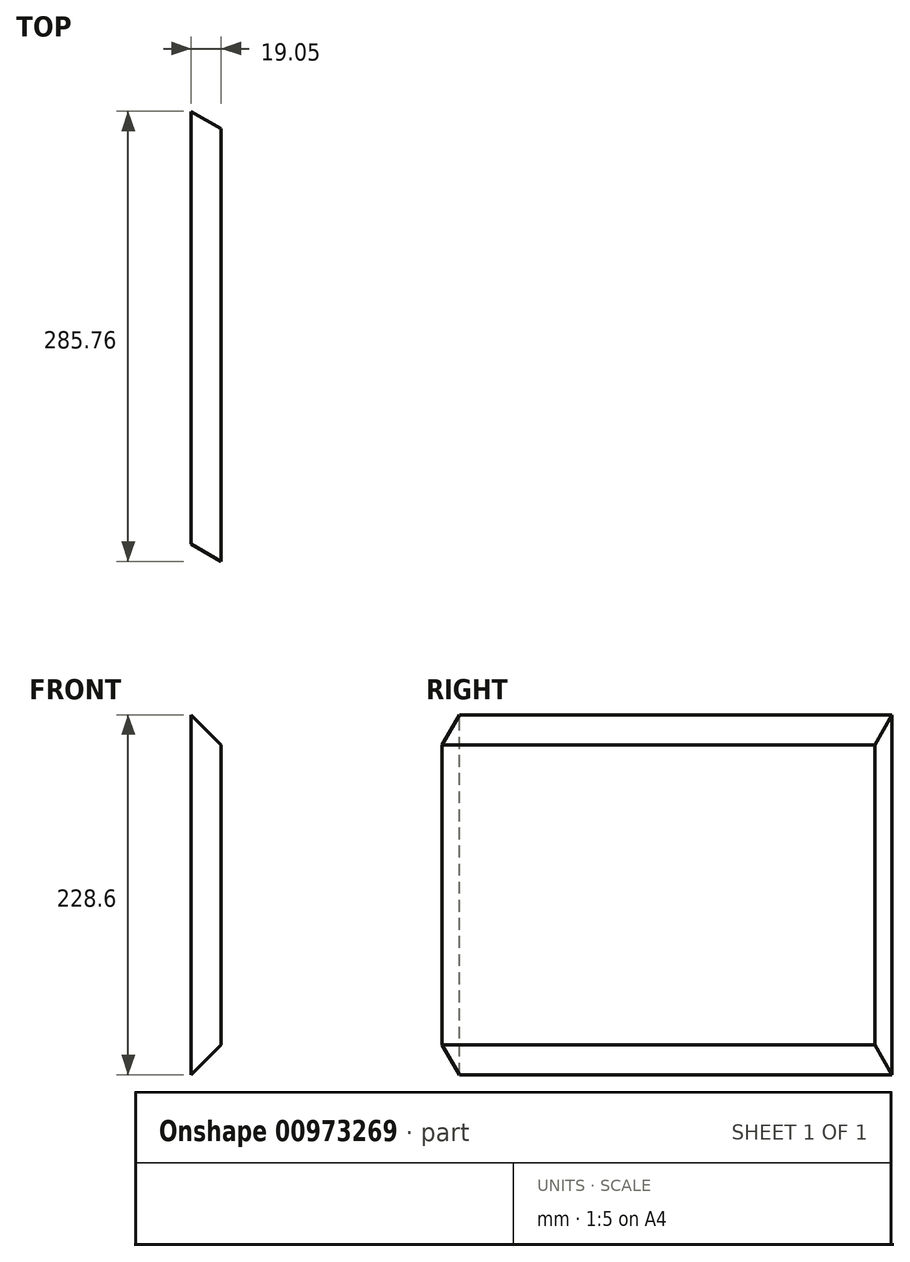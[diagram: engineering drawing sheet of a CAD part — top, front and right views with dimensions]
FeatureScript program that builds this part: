
annotation { "Feature Type Name" : "Feature", "Feature Type Description" : "" }
export const myFeature = defineFeature(function(context is Context, id is Id, definition is map)
    precondition{}
    {
        {
            var Q0;
            Q0=qCreatedBy(makeId("Right.planeOp"),FACE);
            var sketch = newSketch(context, id + "F0", { "sketchPlane" : qUnion([Q0])});
            skLineSegment(sketch, "E0.bottom", {"start": v(142.88, -114.3) * mm, "end": v(-142.88, -114.3) * mm});
            skLineSegment(sketch, "E0.top", {"start": v(142.88, 114.3) * mm, "end": v(-142.88, 114.3) * mm});
            skLineSegment(sketch, "E0.left", {"start": v(142.88, -114.3) * mm, "end": v(142.88, 114.3) * mm});
            skLineSegment(sketch, "E0.right", {"start": v(-142.88, -114.3) * mm, "end": v(-142.88, 114.3) * mm});
            skPoint(sketch, "E0.middle", {"position": v(0, 0) * mm});
            skSolve(sketch);
        }
        {
            var Q0;
            Q0=makeQuery(id+"F0.imprint","IMPRINT",FACE,{"disambiguationData":[TD([[makeQuery(id+"F0.imprint","IMPRINT",EDGE,{"derivedFrom":sQuery(id+"F0.wireOp",EDGE,"E0.bottom")}),-1.0]])]});
            extrude(context, id + "F1", {"entities" : qUnion([Q0]), "depth" : 19.05 * mm, "offsetDistance" : 25.4 * mm});
        }
        {
            var Q0;
            Q0=makeQuery(id+"F1.opExtrude","SWEPT_FACE",FACE,{"disambiguationData":[OSD([sQuery(id+"F0.wireOp",EDGE,"E0.top")])]});
            var sketch = newSketch(context, id + "F2", { "sketchPlane" : qUnion([Q0])});
            skLineSegment(sketch, "E1", {"start": v(19.05, -142.88) * mm, "end": v(0, -131.88) * mm});
            skLineSegment(sketch, "E2", {"start": v(0, -131.88) * mm, "end": v(0, -142.88) * mm});
            skLineSegment(sketch, "E3", {"start": v(0, -142.88) * mm, "end": v(19.05, -142.88) * mm});
            skLineSegment(sketch, "E4", {"start": v(0, 142.88) * mm, "end": v(19.05, 131.88) * mm});
            skLineSegment(sketch, "E5", {"start": v(19.05, 131.88) * mm, "end": v(19.05, 142.88) * mm});
            skLineSegment(sketch, "E6", {"start": v(19.05, 142.88) * mm, "end": v(0, 142.88) * mm});
            skSolve(sketch);
        }
        {
            var Q0;
            Q0 = qSketchRegion(id + "F2", true);
            extrude(context, id + "F3", {"entities" : qUnion([Q0]), "operationType" : NewBodyOperationType.REMOVE, "endBound" : BoundingType.THROUGH_ALL, "oppositeDirection" : true, "depth" : 25.4 * mm, "offsetDistance" : 25.4 * mm});
        }
        {
            var Q0;
            Q0=makeQuery(id+"F1.opExtrude","CAP_EDGE",EDGE,{"disambiguationData":[OSD([sQuery(id+"F0.wireOp",EDGE,"E0.top")])],"isStart":false});
            var Q1;
            Q1=makeQuery(id+"F1.opExtrude","CAP_EDGE",EDGE,{"disambiguationData":[OSD([sQuery(id+"F0.wireOp",EDGE,"E0.bottom")])],"isStart":false});
            chamfer(context, id + "F4", {"entities" : qUnion([Q0, Q1]), "width" : 19.05 * mm, "tangentPropagation" : true});
        }
    });
